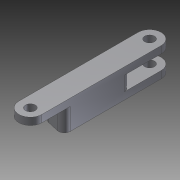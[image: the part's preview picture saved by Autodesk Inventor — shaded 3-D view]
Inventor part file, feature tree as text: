
AUTODESK INVENTOR PART (.ipt)
format: ipt  version: 2011 SP2 (Build 150309200, 309)  size: 130,560 bytes
history: native  units: mm
features: sketch x3, extrude x3, hole x1, fillet x1
ambient origin geometry x8: Origin, YZ Plane, XZ Plane, XY Plane, X Axis, Y Axis, Z Axis, Center Point
feature tree (8):
  sketch  "Sketch1"  dims[d0=4.0mm d6=41.375254mm]
  extrude  "Extrusion5"  Depth=41.375254mm
  extrude  "Extrusion6"  Depth=5.0mm TaperAngle=0.0deg
  hole  "Hole3"  [1 undecoded]
  fillet  "Fillet1"  Radius=10.0mm
  extrude  "Extrusion7"  [1 undecoded]
  sketch  "Sketch4"  dims[d36=10.0mm d37=0.0mm d38=5.0mm d39=0.0mm]
  sketch  "Sketch5"  dims[d40=3.4mm d41=6.0mm d42=4.4mm d43=3.0mm d44=90.0deg d45=8.0mm d46=20.594885mm d47=2.0mm d48=10.0mm d49=0.0mm]
note: 2 required parameter values undecoded (feature->parameter linkage not recoverable at this tier; creation-order binding heuristic only, values carry confidence <= 0.55)
